# Revit family: Urinal-Wall_Mount-Kohler-Dexter-K_5452-E
name_source: partatom
category: Plumbing Fixtures
revit_build: Autodesk Revit 2015 (Build: 20140606_1530(x64)
units: mm (PartAtom-declared; Revit-internal decimal feet)

## types (8) — shared parameters
ADA Compliant = Yes
Assembly Code = D2010210
CW Connection = Yes
Cold Water Diameter = 0' - 0 3/4"
Default Elevation = 3' - 4 1/2"
Drain Diameter = 0' - 2"
Finish = Vitreous China - Kohler - 0 - White
Flush Rate = 0.125 gpf
HW Connection = No
Height = 1' - 8 3/4"
Keynote = 22 40 00.E7
Length = 0' - 11 3/4"
Manufacturer = Kohler
Pressure = 80.00 psi
Product Documentation Link = http://www.us.kohler.com
Product Page URL = http://www.us.kohler.com
Sanitary Connector = NPT Tap, Sanitary Drain
URL = http://www.us.kohler.com
Vent Connection = Yes
Version = 2014 - v1.0a
Waste Connection = Yes
Width = 1' - 2 3/4"
zero-valued in all types: CWFU, HWFU, WFU

## per-type parameters (varying)
| type | C Spud Location | Cold Water Connector | Constraint | ControlM | Description | Model | Product Name | Spud Rear | Spud Top |
| Rear Spud, 0-White | 360.00° | Inlet Spud, Rear | 1 | 0 | 1-Pint Urinal, with Rear Spud, White | K-5452-ER-0 | Dexter Washdown Wall-mount 0.125 gpf Urinal with Rear Spud | Yes | No |
| Rear Spud, 96-Biscuit | 360.00° | Inlet Spud, Rear | 1 | 96 | 1-Pint Urinal, with Rear Spud, Biscuit | K-5452-ER-96 | Dexter Washdown Wall-mount 0.125 gpf Urinal with Rear Spud | Yes | No |
| Rear Spud, 47-Almond | 360.00° | Inlet Spud, Rear | 1 | 47 | 1-Pint Urinal, with Rear Spud, Almond | K-5452-ER-47 | Dexter Washdown Wall-mount 0.125 gpf Urinal with Rear Spud | Yes | No |
| Rear Spud, 7-Black Black | 360.00° | Inlet Spud, Rear | 1 | 7 | 1-Pint Urinal, with Rear Spud, Black Black | K-5452-ER-7 | Dexter Washdown Wall-mount 0.125 gpf Urinal with Rear Spud | Yes | No |
| Top Spud, 0-White | 90.00° | Inlet Spud, Top | 2 | 0 | 1-Pint Urinal, with Top Spud, White | K-5452-ET-0 | Dexter Washdown Wall-mount 0.125 gpf Urinal with Top Spud | No | Yes |
| Top Spud, 47-Almond | 90.00° | Inlet Spud, Top | 2 | 47 | 1-Pint Urinal, with Top Spud, Almond | K-5452-ET-47 | Dexter Washdown Wall-mount 0.125 gpf Urinal with Top Spud | No | Yes |
| Top Spud, 7-Black Black | 90.00° | Inlet Spud, Top | 2 | 7 | 1-Pint Urinal, with Top Spud, Black Black | K-5452-ET-7 | Dexter Washdown Wall-mount 0.125 gpf Urinal with Top Spud | No | Yes |
| Top Spud, 96-Biscuit | 90.00° | Inlet Spud, Top | 2 | 96 | 1-Pint Urinal, with Top Spud, Biscuit | K-5452-ET-96 | Dexter Washdown Wall-mount 0.125 gpf Urinal with Top Spud | No | Yes |

## geometry (parser evidence)
native form markers: Sweep x4
no freeform markers — native parametric forms only
